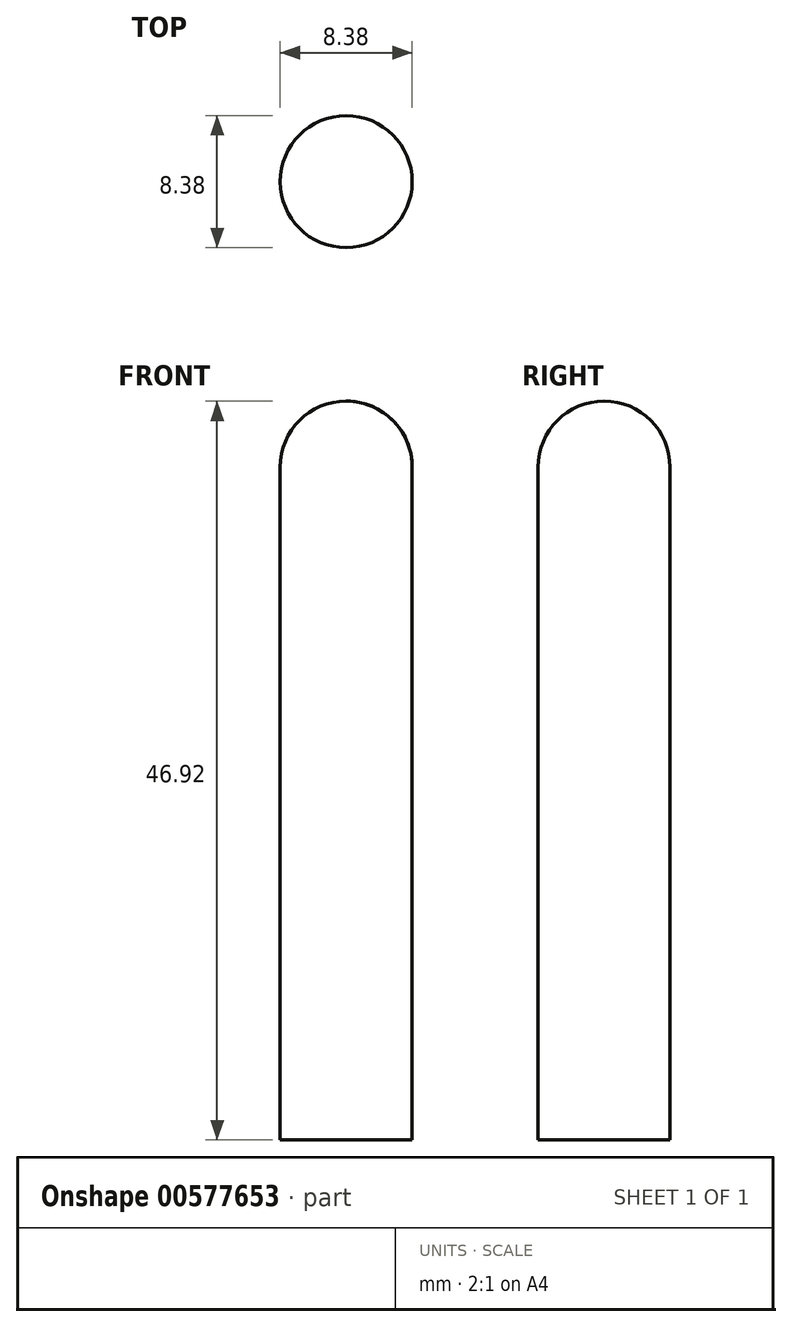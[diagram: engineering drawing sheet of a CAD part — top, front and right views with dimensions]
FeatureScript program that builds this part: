
annotation { "Feature Type Name" : "Feature", "Feature Type Description" : "" }
export const myFeature = defineFeature(function(context is Context, id is Id, definition is map)
    precondition{}
    {
        {
            var Q0;
            Q0=qCreatedBy(makeId("Front.planeOp"),FACE);
            var sketch = newSketch(context, id + "F0", { "sketchPlane" : qUnion([Q0])});
            skLineSegment(sketch, "E0", {"start": v(0, 0) * mm, "end": v(0, 42.73) * mm});
            skLineSegment(sketch, "E1", {"start": v(8.38, 42.73) * mm, "end": v(8.38, 0) * mm});
            skLineSegment(sketch, "E2", {"start": v(8.38, 0) * mm, "end": v(0, 0) * mm});
            skArc(sketch, "E3", {"start": v(8.38, 42.73) * mm, "mid": v(4.2, 46.92) * mm, "end": v(0, 42.73) * mm});
            skLineSegment(sketch, "E4", {"start": v(4.2, 42.73) * mm, "end": v(4.2, -9.93) * mm});
            skLineSegment(sketch, "E5", {"start": v(4.2, -9.93) * mm, "end": v(4.2, 57.8) * mm});
            skPoint(sketch, "E5.endSnap0", {"position": v(4.2, 46.92) * mm});
            skSolve(sketch);
        }
        {
            var Q0;
            {var subQ1=sQuery(id+"F0.wireOp",EDGE,"E1");Q0=makeQuery(id+"F0.imprint","IMPRINT",FACE,{"disambiguationData":[TD([[makeQuery(id+"F0.imprint","IMPRINT",EDGE,{"derivedFrom":subQ1}),-1.0]])]});}
            var Q1;
            Q1=sQuery(id+"F0.wireOp",EDGE,"E5");
            revolve(context, id + "F1", {"entities" : qUnion([Q0]), "axis" : qUnion([Q1]), "revolveType" : RevolveType.FULL});
        }
    });
